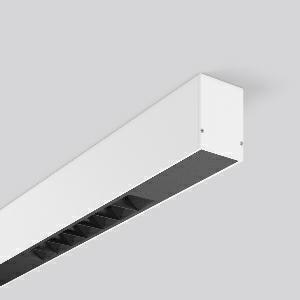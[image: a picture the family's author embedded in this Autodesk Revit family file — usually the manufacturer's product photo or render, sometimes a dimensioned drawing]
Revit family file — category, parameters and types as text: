
# Revit family: less_is_more_beamline_312487_002_b4ea
name_source: partatom
category: Lighting Fixtures
units: mm (PartAtom-declared; Revit-internal decimal feet)

## family parameters
Cut with Voids When Loaded = No
Host = Face
Light Source = No
Part Type = Normal
Room Calculation Point = No
Round Connector Dimension = Use Diameter
Shared = No

## types (1)
- LESS IS MORE BEAMLINE (1 x LED Modul 930, 1750 lm, 3000)
    Apparent Load = 48 VA
    CIE Flux Codes = 100 100 100 100 100
    Color Rendering = 90
    Color Temperature = 3000
    Default Elevation = 1800 mm
    Description = Series: LESS IS MORE BEAMLINE
Linear ceiling and wall luminaire for aesthetically sophisticated lighting. Luminaire with two LED light units. Housing: extruded aluminium profile, powder-coated. End cap aluminium powder-coated. LED light unit with MRS technology: Mini-Reflector-System made of metallised thermoplastic with prismatic black glare-suppressing frame for pleasant glare-free light (RUG < 10). Each LED light unit has 7 reflector elements. Medium beam light distribution. LED unit with integrated converter interchangeable and removable. Suitable for through-wiring. 
Colour: traffic white, matt (RAL 9016)
Length: 1127 mm
Width: 57 mm
Height: 75 mm
Lamp: LED
Socket: without socket
Colour temperature: 3000K
Colour rendering index (CRI): 90
System power: 48 W
Rated luminous flux: 3500 lm
Luminous efficiency: 73 lm/W
Control gear: Regulated power supply
Protection class: I
Type of protection: IP 20
    Height = 75 mm
    Lamp = 1 x LED Modul 930
    Lamp Light Flux = 1750 lm
    Lamp count = 1
    Length = 1127 mm
    Lifetime = 50000 h
    Luminous efficacy = 73 lm/W
    Manufacturer = RZB
    ModVariant = No
    Model = 312487.002
    Mounting Place = Ceiling, Wall
    Mounting Type = Surface mounted
    Number of Poles = 1
    OnlyDefault = Yes
    Power Factor = 1
    Product Name = LESS IS MORE BEAMLINE
    Product group = Surface mounted LED linear luminaires
    ProductGroupID = 307
    Protection Class = Protection class I
    Protection Degree = IP 20
    RLX_Detail_Level = 1
    RLX_Emergency_Light_Flux = 0 lm
    RLX_Emergency_Type = 0
    RLX_Emergency_Type_DB = No
    RlxData = <blob elided: 26913 chars, md5=3b175d28>
    Socket = socket
    Standby Power = 0 W
    System Light Flux = 3500 lm
    System Power = 48 W
    Type Comments = Product without accessories
    Type Image = 312483.002.jpg
    URL = http://relux.com
    VarID = ---
    Voltage = 230 V
    Voltage Range = 220-240 V
    Weight = 0.00 kg
    Width = 57 mm

## geometry (parser evidence)
native form markers: Blend x4, Sweep x14
no freeform markers — native parametric forms only
